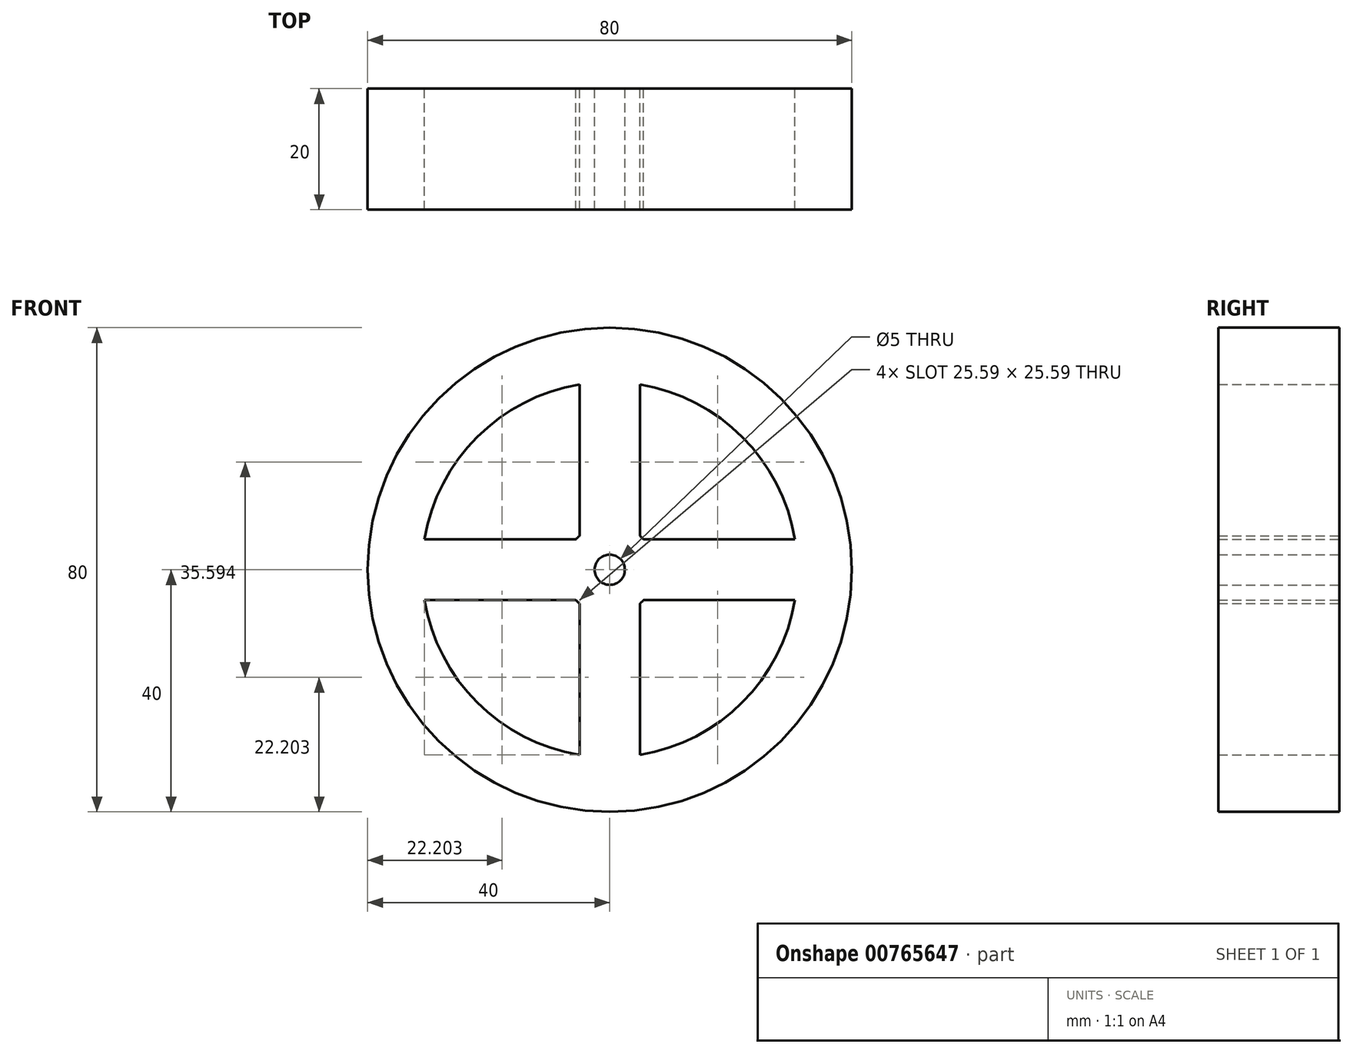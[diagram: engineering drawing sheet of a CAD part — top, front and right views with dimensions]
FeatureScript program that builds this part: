
annotation { "Feature Type Name" : "Feature", "Feature Type Description" : "" }
export const myFeature = defineFeature(function(context is Context, id is Id, definition is map)
    precondition{}
    {
        {
            var Q0;
            Q0=qCreatedBy(makeId("Front.planeOp"),FACE);
            var sketch = newSketch(context, id + "F0", { "sketchPlane" : qUnion([Q0])});
            skCircle(sketch, "E0", {"center": v(0, 0) * mm, "radius": 40 * mm});
            skArc(sketch, "E1", {"start": v(-5, 30.6) * mm, "mid": v(-21.92, 21.92) * mm, "end": v(-30.6, 5) * mm});
            skArc(sketch, "E2", {"start": v(5.6, 5) * mm, "mid": v(5.3, 5.3) * mm, "end": v(5, 5.6) * mm});
            skCircle(sketch, "E3", {"center": v(0, 0) * mm, "radius": 2.5 * mm});
            skLineSegment(sketch, "E4", {"start": v(0, 0) * mm, "end": v(0, -31) * mm, "construction": true});
            skLineSegment(sketch, "E5", {"start": v(0, 31) * mm, "end": v(0, 0) * mm, "construction": true});
            skLineSegment(sketch, "E6", {"start": v(-31, 0) * mm, "end": v(0, 0) * mm, "construction": true});
            skLineSegment(sketch, "E7", {"start": v(0, 0) * mm, "end": v(31, 0) * mm, "construction": true});
            skLineSegment(sketch, "E8.0", {"start": v(-5, 40) * mm, "end": v(-5, 39.69) * mm});
            skLineSegment(sketch, "E9.0", {"start": v(5, 40) * mm, "end": v(5, 39.69) * mm});
            skLineSegment(sketch, "E10.0", {"start": v(5.6, 5) * mm, "end": v(30.6, 5) * mm});
            skLineSegment(sketch, "E11.0", {"start": v(-5, -5.6) * mm, "end": v(-5, -30.6) * mm});
            skLineSegment(sketch, "E12.0", {"start": v(-40, -5) * mm, "end": v(-39.69, -5) * mm});
            skLineSegment(sketch, "E13.0", {"start": v(-40, 5) * mm, "end": v(-39.69, 5) * mm});
            skLineSegment(sketch, "E14.trimOffspring", {"start": v(-5, 30.6) * mm, "end": v(-5, 5.6) * mm});
            skPoint(sketch, "E15.orphan", {"position": v(0, 40) * mm});
            skLineSegment(sketch, "E16.trimOffspring", {"start": v(5, 30.6) * mm, "end": v(5, 5.6) * mm});
            skLineSegment(sketch, "E17.trimOffspring", {"start": v(-30.6, 5) * mm, "end": v(-5.6, 5) * mm});
            skPoint(sketch, "E18.orphan", {"position": v(-40, 0) * mm});
            skLineSegment(sketch, "E19.trimOffspring", {"start": v(-30.6, -5) * mm, "end": v(-5.6, -5) * mm});
            skArc(sketch, "E20.trimOffspring", {"start": v(-30.6, -5) * mm, "mid": v(-21.92, -21.92) * mm, "end": v(-5, -30.6) * mm});
            skLineSegment(sketch, "E21.trimOffspring", {"start": v(39.69, 5) * mm, "end": v(40, 5) * mm});
            skLineSegment(sketch, "E22.trimOffspring", {"start": v(39.69, -5) * mm, "end": v(40, -5) * mm});
            skArc(sketch, "E23.trimOffspring", {"start": v(30.6, 5) * mm, "mid": v(21.92, 21.92) * mm, "end": v(5, 30.6) * mm});
            skLineSegment(sketch, "E24.trimOffspring", {"start": v(-5, -39.69) * mm, "end": v(-5, -40) * mm});
            skLineSegment(sketch, "E25.trimOffspring", {"start": v(5, -39.69) * mm, "end": v(5, -40) * mm});
            skArc(sketch, "E26.trimOffspring", {"start": v(5, -30.6) * mm, "mid": v(21.92, -21.92) * mm, "end": v(30.6, -5) * mm});
            skLineSegment(sketch, "E27.trimOffspring", {"start": v(5, -5.6) * mm, "end": v(5, -30.6) * mm});
            skArc(sketch, "E28.trimOffspring", {"start": v(-5, 5.6) * mm, "mid": v(-5.3, 5.3) * mm, "end": v(-5.6, 5) * mm});
            skArc(sketch, "E29.trimOffspring", {"start": v(-5.6, -5) * mm, "mid": v(-5.3, -5.3) * mm, "end": v(-5, -5.6) * mm});
            skArc(sketch, "E30.trimOffspring", {"start": v(5, -5.6) * mm, "mid": v(5.3, -5.3) * mm, "end": v(5.6, -5) * mm});
            skLineSegment(sketch, "E31.trimOffspring", {"start": v(5.6, -5) * mm, "end": v(30.6, -5) * mm});
            skSolve(sketch);
        }
        {
            var Q0;
            Q0 = qSketchRegion(id + "F0", true);
            extrude(context, id + "F1", {"entities" : qUnion([Q0]), "endBound" : BoundingType.SYMMETRIC, "depth" : 20 * mm, "offsetDistance" : 25.4 * mm});
        }
    });
